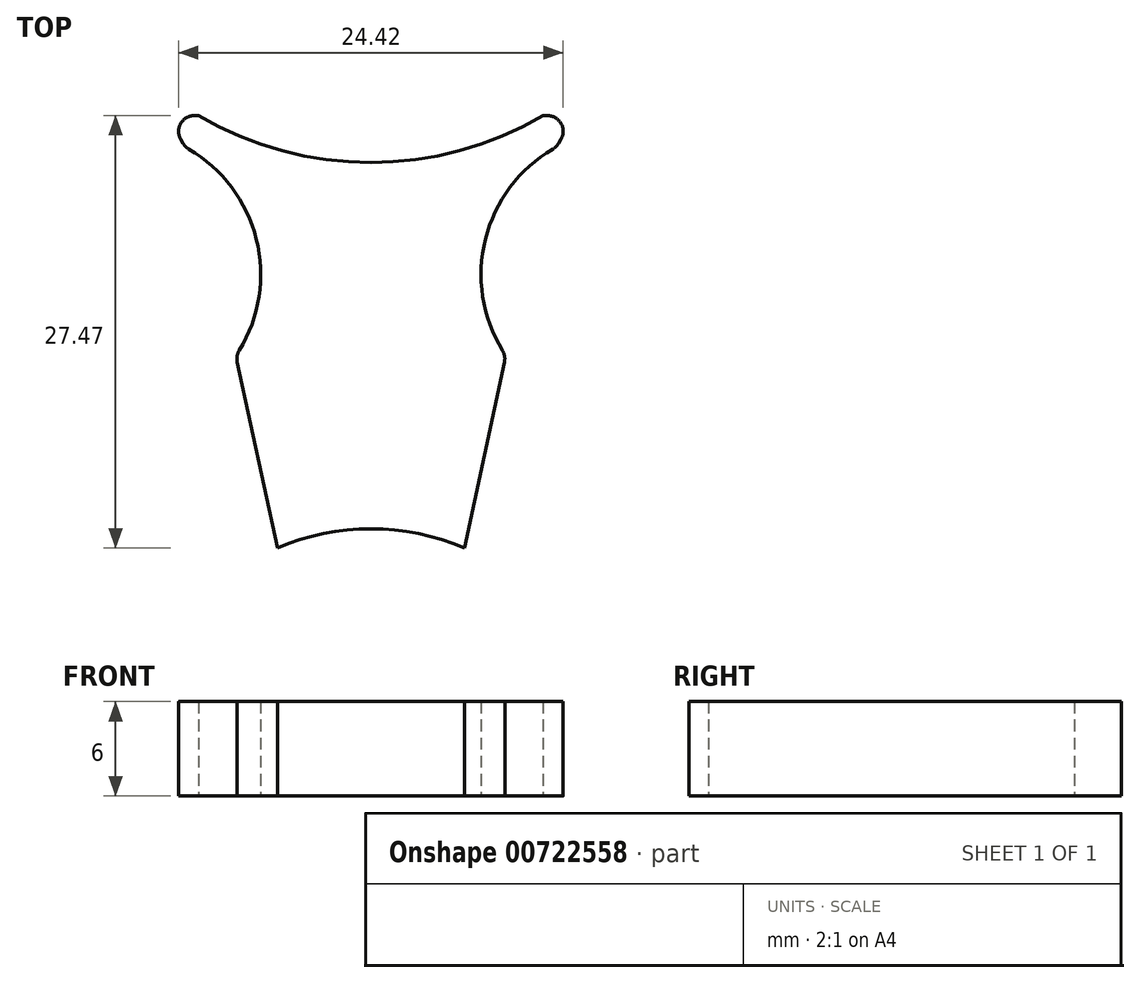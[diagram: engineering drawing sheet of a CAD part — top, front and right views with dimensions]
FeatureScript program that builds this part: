
annotation { "Feature Type Name" : "Feature", "Feature Type Description" : "" }
export const myFeature = defineFeature(function(context is Context, id is Id, definition is map)
    precondition{}
    {
        {
            var Q0;
            Q0=qCreatedBy(makeId("Top.planeOp"),FACE);
            var sketch = newSketch(context, id + "F0", { "sketchPlane" : qUnion([Q0])});
            skLineSegment(sketch, "E0", {"start": v(0, -31.5) * mm, "end": v(0, 39.08) * mm, "construction": true});
            skLineSegment(sketch, "E1", {"start": v(28.67, 0) * mm, "end": v(-28.37, 0) * mm, "construction": true});
            skLineSegment(sketch, "E2.MirrorCS", {"start": v(-11.79, 8.25) * mm, "end": v(-12.95, 10.25) * mm});
            skLineSegment(sketch, "E3.MirrorCS", {"start": v(-12.95, 10.25) * mm, "end": v(-10.95, 10.25) * mm});
            skLineSegment(sketch, "E4.MirrorCS", {"start": v(12.95, 10.25) * mm, "end": v(10.95, 10.25) * mm});
            skLineSegment(sketch, "E5.MirrorCS", {"start": v(11.79, 8.25) * mm, "end": v(12.95, 10.25) * mm});
            skLineSegment(sketch, "E6", {"start": v(-11.79, 8.25) * mm, "end": v(11.79, 8.25) * mm, "construction": true});
            skArc(sketch, "E7", {"start": v(-8.57, -5) * mm, "mid": v(-7.26, 2.33) * mm, "end": v(-11.79, 8.25) * mm});
            skArc(sketch, "E8.MirrorCS", {"start": v(8.57, -5) * mm, "mid": v(7.26, 2.33) * mm, "end": v(11.79, 8.25) * mm});
            skPoint(sketch, "E9.orphan", {"position": v(-7, 0) * mm});
            skPoint(sketch, "E10.orphan", {"position": v(7, 0) * mm});
            skLineSegment(sketch, "E11", {"start": v(-8.57, -5) * mm, "end": v(8.57, -5) * mm, "construction": true});
            skLineSegment(sketch, "E12", {"start": v(-10.95, 14.74) * mm, "end": v(-10.95, 3.9) * mm, "construction": true});
            skLineSegment(sketch, "E13.MirrorCS", {"start": v(10.95, 14.74) * mm, "end": v(10.95, 3.9) * mm, "construction": true});
            skArc(sketch, "E14", {"start": v(-10.95, 10.25) * mm, "mid": v(0, 7.27) * mm, "end": v(10.95, 10.25) * mm});
            skArc(sketch, "E15", {"start": v(5.94, -17.22) * mm, "mid": v(0, -16) * mm, "end": v(-5.94, -17.22) * mm, "construction": true});
            skLineSegment(sketch, "E16", {"start": v(-8.57, -5) * mm, "end": v(-5.94, -17.22) * mm});
            skLineSegment(sketch, "E17.MirrorCS", {"start": v(8.57, -5) * mm, "end": v(5.94, -17.22) * mm});
            skArc(sketch, "E18", {"start": v(5.94, -17.22) * mm, "mid": v(0, -16) * mm, "end": v(-5.94, -17.22) * mm});
            skCircle(sketch, "E19", {"center": v(0, -31) * mm, "radius": 15 * mm, "construction": true});
            skPoint(sketch, "E20", {"position": v(0, -16) * mm});
            skSolve(sketch);
        }
        {
            var Q0;
            Q0=makeQuery(id+"F0.imprint","IMPRINT",FACE,{"disambiguationData":[TD([[makeQuery(id+"F0.imprint","IMPRINT",EDGE,{"derivedFrom":sQuery(id+"F0.wireOp",EDGE,"PfhNlWNs-CzBl-nI37-9E01-fsLF7MDHO91B")}),1.0]])]});
            var Q1;
            Q1=makeQuery(id+"F0.imprint","IMPRINT",FACE,{"disambiguationData":[TD([[makeQuery(id+"F0.imprint","IMPRINT",EDGE,{"derivedFrom":sQuery(id+"F0.wireOp",EDGE,"E2.MirrorCS")}),-1.0]])]});
            extrude(context, id + "F1", {"entities" : qUnion([Q0, Q1]), "endBound" : BoundingType.SYMMETRIC, "depth" : 6 * mm, "offsetDistance" : 25 * mm});
        }
        {
            var Q0;
            Q0=makeQuery(id+"F1.opExtrude","SWEPT_EDGE",EDGE,{"disambiguationData":[OSD([sQuery(id+"F0.wireOp",EDGE,"E2.MirrorCS"),sQuery(id+"F0.wireOp",EDGE,"E3.MirrorCS")])]});
            var Q1;
            Q1=makeQuery(id+"F1.opExtrude","SWEPT_EDGE",EDGE,{"disambiguationData":[OSD([sQuery(id+"F0.wireOp",EDGE,"E4.MirrorCS"),sQuery(id+"F0.wireOp",EDGE,"E5.MirrorCS")])]});
            var Q2;
            Q2=makeQuery(id+"F1.opExtrude","SWEPT_EDGE",EDGE,{"disambiguationData":[OSD([sQuery(id+"F0.wireOp",EDGE,"E7"),sQuery(id+"F0.wireOp",EDGE,"E11")])]});
            var Q3;
            Q3=makeQuery(id+"F1.opExtrude","SWEPT_EDGE",EDGE,{"disambiguationData":[OSD([sQuery(id+"F0.wireOp",EDGE,"E8.MirrorCS"),sQuery(id+"F0.wireOp",EDGE,"E11")])]});
            fillet(context, id + "F2", {"entities" : qUnion([Q0, Q1, Q2, Q3]), "radius" : 1 * mm, "tangentPropagation" : true, "allowEdgeOverflow" : false});
        }
    });
